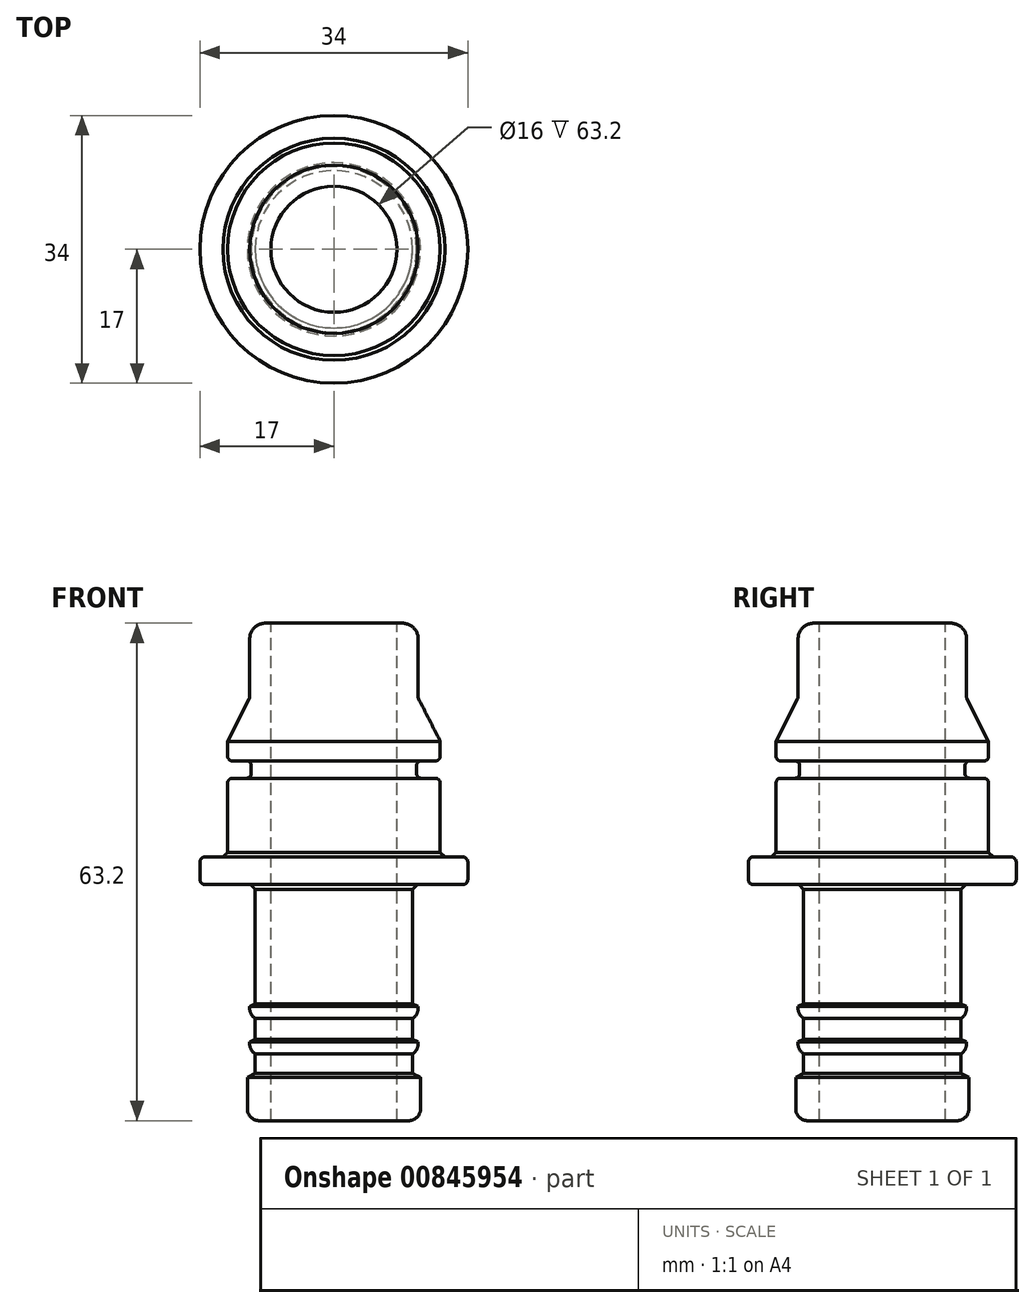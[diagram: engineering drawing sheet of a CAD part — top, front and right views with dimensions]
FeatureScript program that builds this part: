
annotation { "Feature Type Name" : "Feature", "Feature Type Description" : "" }
export const myFeature = defineFeature(function(context is Context, id is Id, definition is map)
    precondition{}
    {
        {
            var Q0;
            Q0=qCreatedBy(makeId("Front.planeOp"),FACE);
            var sketch = newSketch(context, id + "F0", { "sketchPlane" : qUnion([Q0])});
            skLineSegment(sketch, "E0", {"start": v(0, 38.7) * mm, "end": v(-10.7, 38.7) * mm});
            skLineSegment(sketch, "E1", {"start": v(-10.7, 38.7) * mm, "end": v(-10.7, 29.2) * mm});
            skLineSegment(sketch, "E2", {"start": v(-13.5, 23.7) * mm, "end": v(-13.5, 21.2) * mm});
            skLineSegment(sketch, "E3", {"start": v(-10.5, 21.2) * mm, "end": v(-10.5, 19) * mm});
            skLineSegment(sketch, "E4", {"start": v(-13.5, 19) * mm, "end": v(-13.5, 9) * mm});
            skLineSegment(sketch, "E5", {"start": v(-17, 9) * mm, "end": v(-17, 5.5) * mm});
            skLineSegment(sketch, "E6.trimOffspring", {"start": v(-10, 5.5) * mm, "end": v(-10, -9.5) * mm});
            skLineSegment(sketch, "E7", {"start": v(-13.5, 23.7) * mm, "end": v(-10.7, 29.2) * mm});
            skLineSegment(sketch, "E8", {"start": v(-13.5, 21.2) * mm, "end": v(-10.5, 21.2) * mm});
            skLineSegment(sketch, "E9", {"start": v(-13.5, 19) * mm, "end": v(-10.5, 19) * mm});
            skLineSegment(sketch, "E10", {"start": v(-17, 9) * mm, "end": v(-13.5, 9) * mm});
            skLineSegment(sketch, "E11", {"start": v(-17, 5.5) * mm, "end": v(-10, 5.5) * mm});
            skLineSegment(sketch, "E12", {"start": v(-10, -24.5) * mm, "end": v(0, -24.5) * mm});
            skLineSegment(sketch, "E13", {"start": v(0, 38.7) * mm, "end": v(0, -24.5) * mm});
            skLineSegment(sketch, "E14", {"start": v(-10, -24.5) * mm, "end": v(-11, -24.5) * mm});
            skLineSegment(sketch, "E15", {"start": v(-11, -24.5) * mm, "end": v(-11, -18.5) * mm});
            skLineSegment(sketch, "E16", {"start": v(-11, -18.5) * mm, "end": v(-10, -18.5) * mm});
            skLineSegment(sketch, "E17", {"start": v(-10, -16) * mm, "end": v(-10.7, -16) * mm});
            skLineSegment(sketch, "E18", {"start": v(-10.7, -16) * mm, "end": v(-10.7, -14) * mm});
            skLineSegment(sketch, "E19", {"start": v(-10.7, -14) * mm, "end": v(-10, -14) * mm});
            skLineSegment(sketch, "E20", {"start": v(-10, -11.5) * mm, "end": v(-10.7, -11.5) * mm});
            skLineSegment(sketch, "E21", {"start": v(-10.7, -11.5) * mm, "end": v(-10.7, -9.5) * mm});
            skLineSegment(sketch, "E22", {"start": v(-10.7, -9.5) * mm, "end": v(-10, -9.5) * mm});
            skLineSegment(sketch, "E23.trimOffspring", {"start": v(-10, -11.5) * mm, "end": v(-10, -14) * mm});
            skLineSegment(sketch, "E24.trimOffspring", {"start": v(-10, -16) * mm, "end": v(-10, -18.5) * mm});
            skSolve(sketch);
        }
        {
            var Q0;
            Q0 = qSketchRegion(id + "F0", true);
            var Q1;
            Q1=sQuery(id+"F0.wireOp",EDGE,"E13");
            revolve(context, id + "F1", {"surfaceOperationType" : NewSurfaceOperationType.NEW, "entities" : qUnion([Q0]), "axis" : qUnion([Q1]), "revolveType" : RevolveType.FULL});
        }
        {
            var Q0;
            Q0=makeQuery(id+"F1.opRevolve","SWEPT_FACE",FACE,{"disambiguationData":[OSD([sQuery(id+"F0.wireOp",EDGE,"E0")])]});
            var sketch = newSketch(context, id + "F2", { "sketchPlane" : qUnion([Q0])});
            skPoint(sketch, "E25", {"position": v(0, 0) * mm});
            skSolve(sketch);
        }
        {
            var Q0;
            Q0=sQuery(id+"F2.wireOp",VERTEX,"E25");
            var Q1;
            Q1=makeQuery(id+"F1.opRevolve","SWEPT_BODY",BODY,{"disambiguationData":[OSD([sQuery(id+"F0.wireOp",EDGE,"E0"),sQuery(id+"F0.wireOp",EDGE,"E1"),sQuery(id+"F0.wireOp",EDGE,"E2"),sQuery(id+"F0.wireOp",EDGE,"E3"),sQuery(id+"F0.wireOp",EDGE,"E4"),sQuery(id+"F0.wireOp",EDGE,"E5"),sQuery(id+"F0.wireOp",EDGE,"E6.trimOffspring"),sQuery(id+"F0.wireOp",EDGE,"E7"),sQuery(id+"F0.wireOp",EDGE,"E8"),sQuery(id+"F0.wireOp",EDGE,"E9"),sQuery(id+"F0.wireOp",EDGE,"E10"),sQuery(id+"F0.wireOp",EDGE,"E11"),sQuery(id+"F0.wireOp",EDGE,"E12"),sQuery(id+"F0.wireOp",EDGE,"E13")])]});
            hole(context, id + "F3", {"style" : HoleStyle.SIMPLE, "endStyle" : HoleEndStyle.THROUGH, "holeDiameter" : 16 * mm, "majorDiameter" : 5 * mm, "isTappedThrough" : true, "tappedDepth" : 5 * mm, "tapClearance" : 3, "startFromSketch" : true, "locations" : qUnion([Q0]), "scope" : qUnion([Q1])});
        }
        {
            var Q0;
            Q0=makeQuery(id+"F1.opRevolve","SWEPT_EDGE",EDGE,{"disambiguationData":[OSD([sQuery(id+"F0.wireOp",EDGE,"E5"),sQuery(id+"F0.wireOp",EDGE,"E10")])]});
            var Q1;
            Q1=makeQuery(id+"F1.opRevolve","SWEPT_EDGE",EDGE,{"disambiguationData":[OSD([sQuery(id+"F0.wireOp",EDGE,"E5"),sQuery(id+"F0.wireOp",EDGE,"E11")])]});
            var Q2;
            Q2=makeQuery(id+"F1.opRevolve","SWEPT_EDGE",EDGE,{"disambiguationData":[OSD([sQuery(id+"F0.wireOp",EDGE,"E1"),sQuery(id+"F0.wireOp",EDGE,"E7")])]});
            var Q3;
            Q3=makeQuery(id+"F1.opRevolve","SWEPT_EDGE",EDGE,{"disambiguationData":[OSD([sQuery(id+"F0.wireOp",EDGE,"E3"),sQuery(id+"F0.wireOp",EDGE,"E9")])]});
            var Q4;
            Q4=makeQuery(id+"F1.opRevolve","SWEPT_EDGE",EDGE,{"disambiguationData":[OSD([sQuery(id+"F0.wireOp",EDGE,"E3"),sQuery(id+"F0.wireOp",EDGE,"E8")])]});
            var Q5;
            Q5=makeQuery(id+"F1.opRevolve","SWEPT_EDGE",EDGE,{"disambiguationData":[OSD([sQuery(id+"F0.wireOp",EDGE,"E4"),sQuery(id+"F0.wireOp",EDGE,"E9")])]});
            var Q6;
            Q6=makeQuery(id+"F1.opRevolve","SWEPT_EDGE",EDGE,{"disambiguationData":[OSD([sQuery(id+"F0.wireOp",EDGE,"E2"),sQuery(id+"F0.wireOp",EDGE,"E8")])]});
            fillet(context, id + "F4", {"entities" : qUnion([Q0, Q1, Q2, Q3, Q4, Q5, Q6]), "radius" : 0.6 * mm, "tangentPropagation" : true, "allowEdgeOverflow" : false});
        }
        {
            var Q0;
            Q0=makeQuery(id+"F3.hole-0.boolean.opBoolean","COPY",EDGE,{"derivedFrom":makeQuery(id+"F3.hole-0.opRevolve","SWEPT_EDGE",EDGE,{"disambiguationData":[OSD([sQuery(id+"F3.hole-0.sketch.wireOp",EDGE,"core_line_2"),sQuery(id+"F3.hole-0.sketch.wireOp",EDGE,"core_line_3")])]})});
            var Q1;
            Q1=makeQuery(id+"F1.opRevolve","SWEPT_EDGE",EDGE,{"disambiguationData":[OSD([sQuery(id+"F0.wireOp",EDGE,"E4"),sQuery(id+"F0.wireOp",EDGE,"E10")])]});
            var Q2;
            Q2=makeQuery(id+"F1.opRevolve","SWEPT_EDGE",EDGE,{"disambiguationData":[OSD([sQuery(id+"F0.wireOp",EDGE,"E6.trimOffspring"),sQuery(id+"F0.wireOp",EDGE,"E11")])]});
            var Q3;
            Q3=makeQuery(id+"F3.hole-0.boolean.opBoolean","INTERSECT",EDGE,{"derivedFrom":[makeQuery(id+"F1.opRevolve","SWEPT_FACE",FACE,{"disambiguationData":[OSD([sQuery(id+"F0.wireOp",EDGE,"E12"),sQuery(id+"F0.wireOp",EDGE,"E14")])]}),makeQuery(id+"F3.hole-0.opRevolve","SWEPT_FACE",FACE,{"disambiguationData":[OSD([sQuery(id+"F3.hole-0.sketch.wireOp",EDGE,"core_line_2")])]})]});
            chamfer(context, id + "F5", {"entities" : qUnion([Q0, Q1, Q2, Q3]), "width" : 0.6 * mm, "tangentPropagation" : true});
        }
        {
            var Q0;
            Q0=makeQuery(id+"F1.opRevolve","SWEPT_EDGE",EDGE,{"disambiguationData":[OSD([sQuery(id+"F0.wireOp",EDGE,"E14"),sQuery(id+"F0.wireOp",EDGE,"E15")])]});
            var Q1;
            Q1=makeQuery(id+"F1.opRevolve","SWEPT_EDGE",EDGE,{"disambiguationData":[OSD([sQuery(id+"F0.wireOp",EDGE,"E17"),sQuery(id+"F0.wireOp",EDGE,"E18")])]});
            var Q2;
            Q2=makeQuery(id+"F1.opRevolve","SWEPT_EDGE",EDGE,{"disambiguationData":[OSD([sQuery(id+"F0.wireOp",EDGE,"E20"),sQuery(id+"F0.wireOp",EDGE,"E21")])]});
            fillet(context, id + "F6", {"entities" : qUnion([Q0, Q1, Q2]), "radius" : 1.5 * mm, "tangentPropagation" : true, "allowEdgeOverflow" : false});
        }
        {
            var Q0;
            Q0=makeQuery(id+"F1.opRevolve","SWEPT_EDGE",EDGE,{"disambiguationData":[OSD([sQuery(id+"F0.wireOp",EDGE,"E15"),sQuery(id+"F0.wireOp",EDGE,"E16")])]});
            var Q1;
            Q1=makeQuery(id+"F1.opRevolve","SWEPT_EDGE",EDGE,{"disambiguationData":[OSD([sQuery(id+"F0.wireOp",EDGE,"E18"),sQuery(id+"F0.wireOp",EDGE,"E19")])]});
            var Q2;
            Q2=makeQuery(id+"F1.opRevolve","SWEPT_EDGE",EDGE,{"disambiguationData":[OSD([sQuery(id+"F0.wireOp",EDGE,"E21"),sQuery(id+"F0.wireOp",EDGE,"E22")])]});
            chamfer(context, id + "F7", {"entities" : qUnion([Q0, Q1, Q2]), "chamferType" : ChamferType.TWO_OFFSETS, "width1" : 1 * mm, "oppositeDirection" : false, "width2" : 0.5 * mm, "tangentPropagation" : true});
        }
        {
            var Q0;
            Q0=makeQuery(id+"F1.opRevolve","SWEPT_EDGE",EDGE,{"disambiguationData":[OSD([sQuery(id+"F0.wireOp",EDGE,"E0"),sQuery(id+"F0.wireOp",EDGE,"E1")])]});
            fillet(context, id + "F8", {"entities" : qUnion([Q0]), "radius" : 2 * mm, "tangentPropagation" : true, "allowEdgeOverflow" : false});
        }
    });
